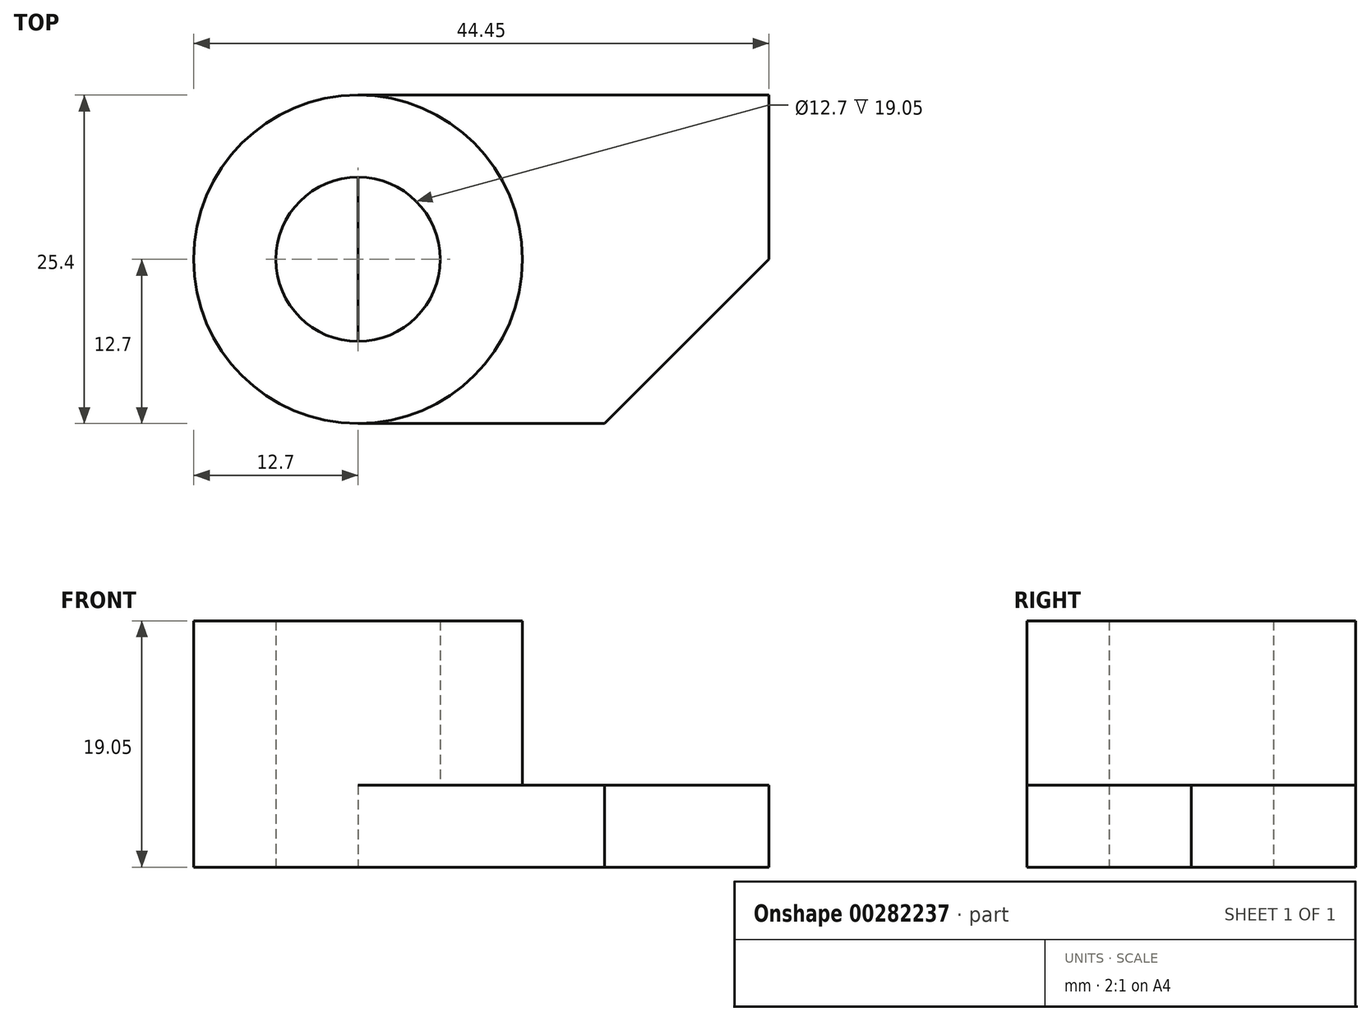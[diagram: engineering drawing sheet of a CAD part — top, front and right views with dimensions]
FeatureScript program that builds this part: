
annotation { "Feature Type Name" : "Feature", "Feature Type Description" : "" }
export const myFeature = defineFeature(function(context is Context, id is Id, definition is map)
    precondition{}
    {
        {
            var Q0;
            Q0=qCreatedBy(makeId("Top.planeOp"),FACE);
            var sketch = newSketch(context, id + "F0", { "sketchPlane" : qUnion([Q0])});
            skCircle(sketch, "E0", {"center": v(0, 0) * mm, "radius": 12.7 * mm});
            skCircle(sketch, "E1", {"center": v(0, 0) * mm, "radius": 6.35 * mm});
            skSolve(sketch);
        }
        {
            var Q0;
            Q0 = qSketchRegion(id + "F0", true);
            extrude(context, id + "F1", {"entities" : qUnion([Q0]), "depth" : 19.05 * mm});
        }
        {
            var Q0;
            Q0=qCreatedBy(makeId("Front.planeOp"),FACE);
            var sketch = newSketch(context, id + "F2", { "sketchPlane" : qUnion([Q0])});
            skLineSegment(sketch, "E2.bottom", {"start": v(0, 0) * mm, "end": v(31.75, 0) * mm});
            skLineSegment(sketch, "E2.top", {"start": v(0, 6.35) * mm, "end": v(31.75, 6.35) * mm});
            skLineSegment(sketch, "E2.left", {"start": v(0, 0) * mm, "end": v(0, 6.35) * mm});
            skLineSegment(sketch, "E2.right", {"start": v(31.75, 0) * mm, "end": v(31.75, 6.35) * mm});
            skSolve(sketch);
        }
        {
            var Q0;
            Q0 = qSketchRegion(id + "F2", true);
            extrude(context, id + "F3", {"entities" : qUnion([Q0]), "operationType" : NewBodyOperationType.ADD, "endBound" : BoundingType.SYMMETRIC, "depth" : 25.4 * mm});
        }
        {
            var Q0;
            {var subQ2=sQuery(id+"F2.wireOp",EDGE,"E2.top");Q0=makeQuery(id+"F3.boolean.opBoolean","SPLIT",FACE,{"disambiguationData":[TD([makeQuery(id+"F1.opExtrude","SWEPT_FACE",FACE,{"disambiguationData":[OSD([sQuery(id+"F0.wireOp",EDGE,"E0")])]})])],"derivedFrom":makeQuery(id+"F3.opExtrude","SWEPT_FACE",FACE,{"disambiguationData":[OSD([subQ2])]})});}
            var sketch = newSketch(context, id + "F4", { "sketchPlane" : qUnion([Q0])});
            skLineSegment(sketch, "E3", {"start": v(31.75, 0) * mm, "end": v(31.75, -12.7) * mm});
            skLineSegment(sketch, "E4", {"start": v(31.75, -12.7) * mm, "end": v(19.05, -12.7) * mm});
            skLineSegment(sketch, "E5", {"start": v(19.05, -12.7) * mm, "end": v(31.75, 0) * mm});
            skSolve(sketch);
        }
        {
            var Q0;
            Q0=makeQuery(id+"F4.imprint","IMPRINT",FACE,{"disambiguationData":[TD([[makeQuery(id+"F4.imprint","IMPRINT",EDGE,{"derivedFrom":sQuery(id+"F4.wireOp",EDGE,"E3")}),1.0]])]});
            extrude(context, id + "F5", {"entities" : qUnion([Q0]), "operationType" : NewBodyOperationType.REMOVE, "oppositeDirection" : true, "depth" : 6.35 * mm});
        }
    });
